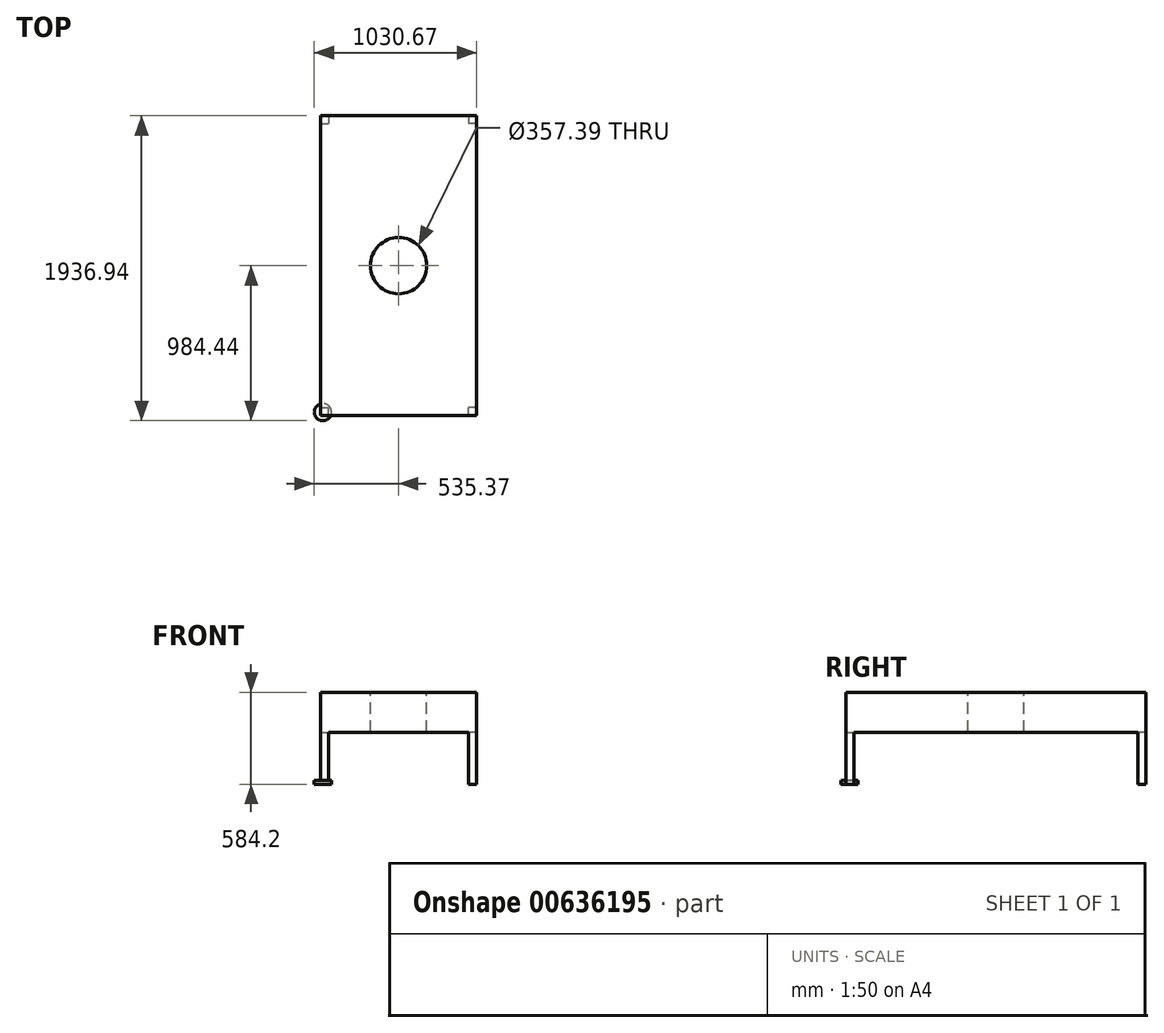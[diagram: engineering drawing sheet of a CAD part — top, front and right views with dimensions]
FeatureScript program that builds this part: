
annotation { "Feature Type Name" : "Feature", "Feature Type Description" : "" }
export const myFeature = defineFeature(function(context is Context, id is Id, definition is map)
    precondition{}
    {
        {
            var Q0;
            Q0=qCreatedBy(makeId("Top.planeOp"),FACE);
            var sketch = newSketch(context, id + "F0", { "sketchPlane" : qUnion([Q0])});
            skLineSegment(sketch, "E0.bottom", {"start": v(495.3, 952.5) * mm, "end": v(-495.3, 952.5) * mm});
            skLineSegment(sketch, "E0.top", {"start": v(495.3, -952.5) * mm, "end": v(-495.3, -952.5) * mm});
            skLineSegment(sketch, "E0.left", {"start": v(495.3, 952.5) * mm, "end": v(495.3, -952.5) * mm});
            skLineSegment(sketch, "E0.right", {"start": v(-495.3, 952.5) * mm, "end": v(-495.3, -952.5) * mm});
            skPoint(sketch, "E0.middle", {"position": v(0, 0) * mm});
            skSolve(sketch);
        }
        {
            var Q0;
            Q0 = qSketchRegion(id + "F0", true);
            extrude(context, id + "F1", {"entities" : qUnion([Q0]), "depth" : 254 * mm, "offsetDistance" : 25.4 * mm});
        }
        {
            var Q0;
            Q0=makeQuery(id+"F1.opExtrude","CAP_FACE",FACE,{"disambiguationData":[OSD([sQuery(id+"F0.wireOp",EDGE,"E0.bottom"),sQuery(id+"F0.wireOp",EDGE,"E0.top"),sQuery(id+"F0.wireOp",EDGE,"E0.left"),sQuery(id+"F0.wireOp",EDGE,"E0.right")])],"isStart":true});
            var sketch = newSketch(context, id + "F2", { "sketchPlane" : qUnion([Q0])});
            skLineSegment(sketch, "E1.bottom", {"start": v(-495.3, 952.5) * mm, "end": v(-444.5, 952.5) * mm});
            skLineSegment(sketch, "E1.top", {"start": v(-495.3, 901.7) * mm, "end": v(-444.5, 901.7) * mm});
            skLineSegment(sketch, "E1.left", {"start": v(-495.3, 952.5) * mm, "end": v(-495.3, 901.7) * mm});
            skLineSegment(sketch, "E1.right", {"start": v(-444.5, 952.5) * mm, "end": v(-444.5, 901.7) * mm});
            skSolve(sketch);
        }
        {
            var Q0;
            Q0=makeQuery(id+"F2.imprint","IMPRINT",FACE,{"disambiguationData":[TD([[makeQuery(id+"F2.imprint","IMPRINT",EDGE,{"derivedFrom":sQuery(id+"F2.wireOp",EDGE,"E1.bottom")}),1.0]])]});
            var Q1;
            Q1 = qSketchRegion(id + "F2", true);
            extrude(context, id + "F3", {"entities" : qUnion([Q0, Q1]), "operationType" : NewBodyOperationType.ADD, "depth" : 330.2 * mm, "offsetDistance" : 25.4 * mm});
        }
        {
            var Q0;
            Q0=makeQuery(id+"F1.opExtrude","SWEPT_BODY",BODY,{"disambiguationData":[OSD([sQuery(id+"F0.wireOp",EDGE,"E0.bottom"),sQuery(id+"F0.wireOp",EDGE,"E0.top"),sQuery(id+"F0.wireOp",EDGE,"E0.left"),sQuery(id+"F0.wireOp",EDGE,"E0.right")])]});
            var Q1;
            Q1=qCreatedBy(makeId("Right.planeOp"),FACE);
            mirror(context, id + "F4", {"operationType" : NewBodyOperationType.ADD, "entities" : qUnion([Q0]), "mirrorPlane" : qUnion([Q1])});
        }
        {
            var Q0;
            Q0=makeQuery(id+"F1.opExtrude","SWEPT_BODY",BODY,{"disambiguationData":[OSD([sQuery(id+"F0.wireOp",EDGE,"E0.bottom"),sQuery(id+"F0.wireOp",EDGE,"E0.top"),sQuery(id+"F0.wireOp",EDGE,"E0.left"),sQuery(id+"F0.wireOp",EDGE,"E0.right")])]});
            var Q1;
            Q1=qCreatedBy(makeId("Front.planeOp"),FACE);
            mirror(context, id + "F5", {"operationType" : NewBodyOperationType.ADD, "entities" : qUnion([Q0]), "mirrorPlane" : qUnion([Q1])});
        }
        {
            var Q0;
            Q0=makeQuery(id+"F1.opExtrude","CAP_FACE",FACE,{"disambiguationData":[OSD([sQuery(id+"F0.wireOp",EDGE,"E0.bottom"),sQuery(id+"F0.wireOp",EDGE,"E0.top"),sQuery(id+"F0.wireOp",EDGE,"E0.left"),sQuery(id+"F0.wireOp",EDGE,"E0.right")])],"isStart":false});
            var sketch = newSketch(context, id + "F6", { "sketchPlane" : qUnion([Q0])});
            skCircle(sketch, "E2", {"center": v(0, 0) * mm, "radius": 178.7 * mm});
            skSolve(sketch);
        }
        {
            var Q0;
            Q0=makeQuery(id+"F6.imprint","IMPRINT",FACE,{"disambiguationData":[TD([[makeQuery(id+"F6.imprint","IMPRINT",EDGE,{"derivedFrom":sQuery(id+"F6.wireOp",EDGE,"E2")}),1.0]])]});
            var Q1;
            Q1=sQuery(id+"F6.wireOp",EDGE,"E2");
            extrude(context, id + "F7", {"entities" : qUnion([Q0]), "operationType" : NewBodyOperationType.REMOVE, "surfaceEntities" : qUnion([Q1]), "endBound" : BoundingType.THROUGH_ALL, "oppositeDirection" : true, "depth" : 25.4 * mm, "offsetDistance" : 25.4 * mm});
        }
        {
            var Q0;
            Q0=makeQuery(id+"F3.opExtrude","CAP_FACE",FACE,{"disambiguationData":[OSD([sQuery(id+"F2.wireOp",EDGE,"E1.bottom"),sQuery(id+"F2.wireOp",EDGE,"E1.top"),sQuery(id+"F2.wireOp",EDGE,"E1.left"),sQuery(id+"F2.wireOp",EDGE,"E1.right")])],"isStart":false});
            var sketch = newSketch(context, id + "F8", { "sketchPlane" : qUnion([Q0])});
            skCircle(sketch, "E3", {"center": v(-480.84, 929.9) * mm, "radius": 54.53 * mm});
            skSolve(sketch);
        }
        {
            var Q0;
            Q0 = qSketchRegion(id + "F8", true);
            extrude(context, id + "F9", {"entities" : qUnion([Q0]), "operationType" : NewBodyOperationType.ADD, "oppositeDirection" : true, "depth" : 25.4 * mm, "offsetDistance" : 25.4 * mm});
        }
    });
